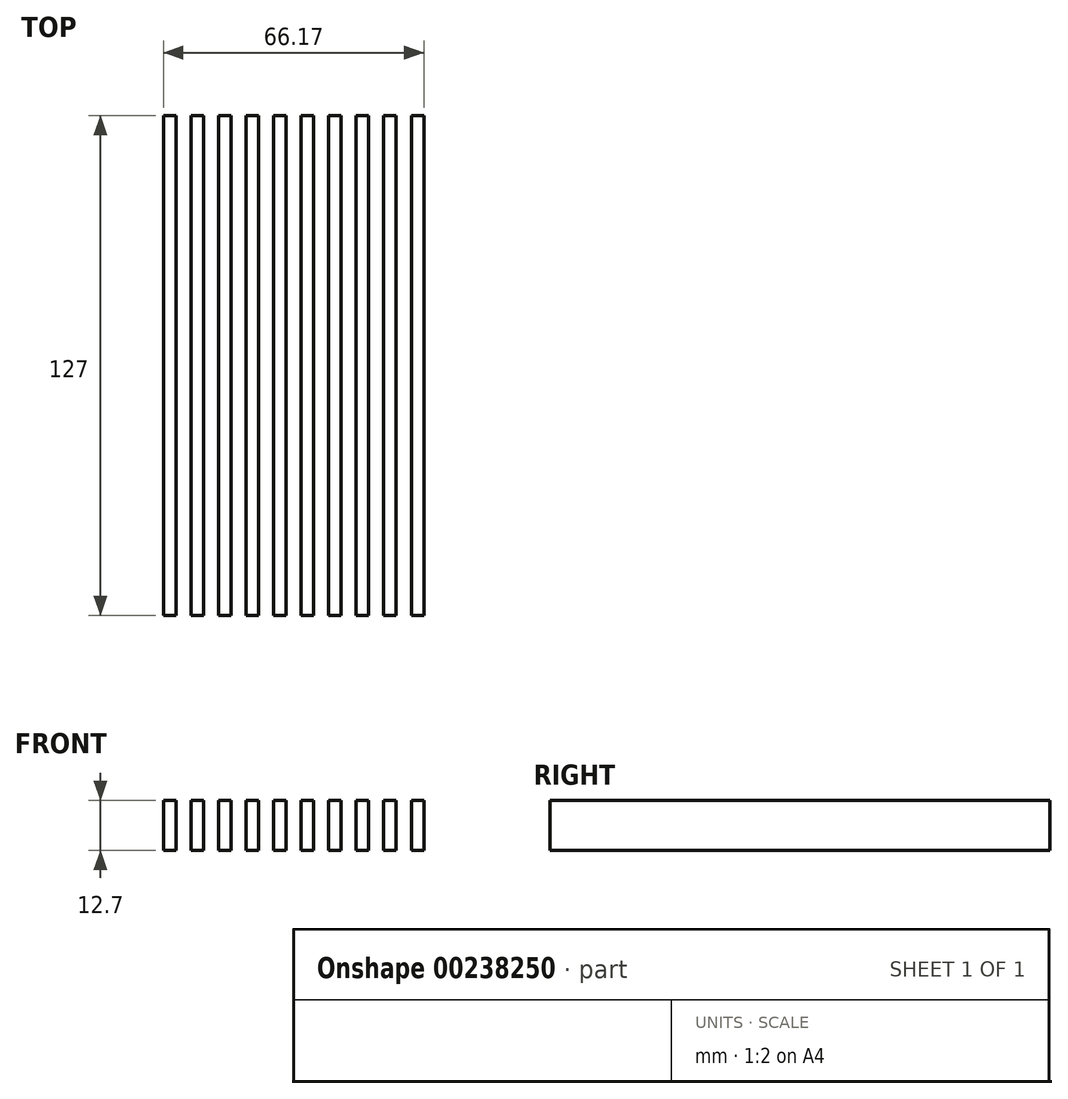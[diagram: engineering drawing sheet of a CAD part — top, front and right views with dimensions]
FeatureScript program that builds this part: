
annotation { "Feature Type Name" : "Feature", "Feature Type Description" : "" }
export const myFeature = defineFeature(function(context is Context, id is Id, definition is map)
    precondition{}
    {
        {
            var Q0;
            Q0=qCreatedBy(makeId("Front.planeOp"),FACE);
            var sketch = newSketch(context, id + "F0", { "sketchPlane" : qUnion([Q0])});
            skLineSegment(sketch, "E0.bottom", {"start": v(0, 0) * mm, "end": v(3.18, 0) * mm});
            skLineSegment(sketch, "E0.top", {"start": v(0, 12.7) * mm, "end": v(3.17, 12.7) * mm});
            skLineSegment(sketch, "E0.left", {"start": v(0, 0) * mm, "end": v(0, 12.7) * mm});
            skLineSegment(sketch, "E0.right", {"start": v(3.18, 0) * mm, "end": v(3.18, 12.7) * mm});
            skLineSegment(sketch, "E1.1.0.0", {"start": v(7, 12.7) * mm, "end": v(10.17, 12.7) * mm});
            skLineSegment(sketch, "E1.1.0.1", {"start": v(7, 0) * mm, "end": v(7, 12.7) * mm});
            skLineSegment(sketch, "E1.1.0.2", {"start": v(10.18, 0) * mm, "end": v(10.18, 12.7) * mm});
            skLineSegment(sketch, "E1.1.0.3", {"start": v(7, 0) * mm, "end": v(10.18, 0) * mm});
            skLineSegment(sketch, "E1.2.0.0", {"start": v(14, 12.7) * mm, "end": v(17.17, 12.7) * mm});
            skLineSegment(sketch, "E1.2.0.1", {"start": v(14, 0) * mm, "end": v(14, 12.7) * mm});
            skLineSegment(sketch, "E1.2.0.2", {"start": v(17.18, 0) * mm, "end": v(17.18, 12.7) * mm});
            skLineSegment(sketch, "E1.2.0.3", {"start": v(14, 0) * mm, "end": v(17.18, 0) * mm});
            skLineSegment(sketch, "E1.3.0.0", {"start": v(21, 12.7) * mm, "end": v(24.17, 12.7) * mm});
            skLineSegment(sketch, "E1.3.0.1", {"start": v(21, 0) * mm, "end": v(21, 12.7) * mm});
            skLineSegment(sketch, "E1.3.0.2", {"start": v(24.18, 0) * mm, "end": v(24.18, 12.7) * mm});
            skLineSegment(sketch, "E1.3.0.3", {"start": v(21, 0) * mm, "end": v(24.17, 0) * mm});
            skLineSegment(sketch, "E1.4.0.0", {"start": v(28, 12.7) * mm, "end": v(31.17, 12.7) * mm});
            skLineSegment(sketch, "E1.4.0.1", {"start": v(28, 0) * mm, "end": v(28, 12.7) * mm});
            skLineSegment(sketch, "E1.4.0.2", {"start": v(31.18, 0) * mm, "end": v(31.18, 12.7) * mm});
            skLineSegment(sketch, "E1.4.0.3", {"start": v(28, 0) * mm, "end": v(31.17, 0) * mm});
            skLineSegment(sketch, "E1.5.0.0", {"start": v(35, 12.7) * mm, "end": v(38.17, 12.7) * mm});
            skLineSegment(sketch, "E1.5.0.1", {"start": v(35, 0) * mm, "end": v(35, 12.7) * mm});
            skLineSegment(sketch, "E1.5.0.2", {"start": v(38.17, 0) * mm, "end": v(38.17, 12.7) * mm});
            skLineSegment(sketch, "E1.5.0.3", {"start": v(35, 0) * mm, "end": v(38.17, 0) * mm});
            skLineSegment(sketch, "E1.6.0.0", {"start": v(42, 12.7) * mm, "end": v(45.17, 12.7) * mm});
            skLineSegment(sketch, "E1.6.0.1", {"start": v(42, 0) * mm, "end": v(42, 12.7) * mm});
            skLineSegment(sketch, "E1.6.0.2", {"start": v(45.17, 0) * mm, "end": v(45.17, 12.7) * mm});
            skLineSegment(sketch, "E1.6.0.3", {"start": v(42, 0) * mm, "end": v(45.17, 0) * mm});
            skLineSegment(sketch, "E1.7.0.0", {"start": v(49, 12.7) * mm, "end": v(52.17, 12.7) * mm});
            skLineSegment(sketch, "E1.7.0.1", {"start": v(49, 0) * mm, "end": v(49, 12.7) * mm});
            skLineSegment(sketch, "E1.7.0.2", {"start": v(52.17, 0) * mm, "end": v(52.17, 12.7) * mm});
            skLineSegment(sketch, "E1.7.0.3", {"start": v(49, 0) * mm, "end": v(52.17, 0) * mm});
            skLineSegment(sketch, "E1.8.0.0", {"start": v(56, 12.7) * mm, "end": v(59.17, 12.7) * mm});
            skLineSegment(sketch, "E1.8.0.1", {"start": v(56, 0) * mm, "end": v(56, 12.7) * mm});
            skLineSegment(sketch, "E1.8.0.2", {"start": v(59.17, 0) * mm, "end": v(59.17, 12.7) * mm});
            skLineSegment(sketch, "E1.8.0.3", {"start": v(56, 0) * mm, "end": v(59.17, 0) * mm});
            skLineSegment(sketch, "E1.9.0.0", {"start": v(63, 12.7) * mm, "end": v(66.17, 12.7) * mm});
            skLineSegment(sketch, "E1.9.0.1", {"start": v(63, 0) * mm, "end": v(63, 12.7) * mm});
            skLineSegment(sketch, "E1.9.0.2", {"start": v(66.17, 0) * mm, "end": v(66.17, 12.7) * mm});
            skLineSegment(sketch, "E1.9.0.3", {"start": v(63, 0) * mm, "end": v(66.18, 0) * mm});
            skLineSegment(sketch, "E1.direction1", {"start": v(0, 0) * mm, "end": v(7, 0) * mm, "construction": true});
            skSolve(sketch);
        }
        {
            var Q0;
            Q0=qSketchRegion(id+"F0",true);
            extrude(context, id + "F1", {"entities" : qUnion([Q0]), "depth" : 127 * mm});
        }
    });
